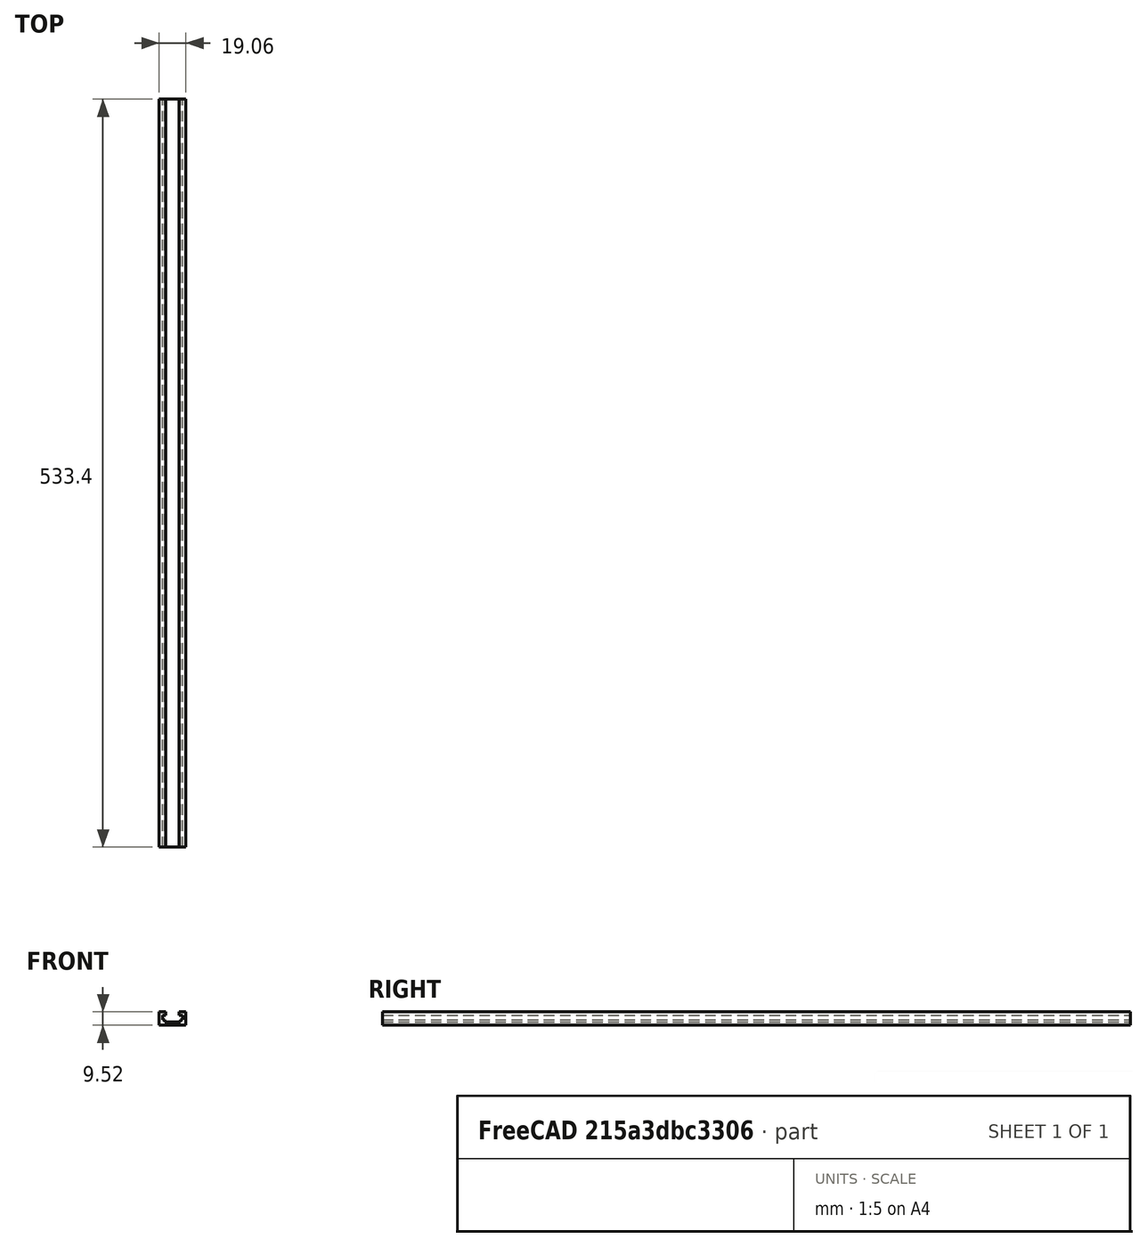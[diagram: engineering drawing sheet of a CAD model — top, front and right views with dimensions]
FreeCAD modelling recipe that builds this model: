
FCSTD DOCUMENT  (FreeCAD 0.20R29603 (Git))
Label: near_fence_top_t_track
License: All rights reserved
LicenseURL: http://en.wikipedia.org/wiki/All_rights_reserved
objects: Sketcher::SketchObject×4, PartDesign::Pocket×3, TechDraw::DrawProjGroupItem×2, PartDesign::Pad×1, PartDesign::Body×1, TechDraw::DrawSVGTemplate×1, TechDraw::DrawProjGroup×1, TechDraw::DrawViewDimension×1, TechDraw::DrawPage×1
note: 13 computed .brp shape members not serialized (recipe doc carries the construction recipe); baked Part::Feature solids carry a one-line shape summary decoded from their .brp

FEATURE [Sketcher::SketchObject] Sketch
  FullyConstrained = true
  MapMode = 5
  Placement = pos=(0,0,0) rot=(1,0,0;1.5708rad)
  Support = -> [XZ_Plane]
  sketch-geometry (5):
    g0: LineSegment StartX=-9.525 StartY=-4.7625 StartZ=0 EndX=-9.525 EndY=4.7625 EndZ=0
    g1: LineSegment StartX=-9.525 StartY=4.7625 StartZ=0 EndX=9.525 EndY=4.7625 EndZ=0
    g2: LineSegment StartX=9.525 StartY=4.7625 StartZ=0 EndX=9.525 EndY=-4.7625 EndZ=0
    g3: LineSegment StartX=9.525 StartY=-4.7625 StartZ=0 EndX=-9.525 EndY=-4.7625 EndZ=0
    g4: GeomPoint X=0 Y=0 Z=0
  constraints (12):
    c: Coincident(g0,g1)
    c: Coincident(g1,g2)
    c: Coincident(g2,g3)
    c: Coincident(g3,g0)
    c: Horizontal(g1)
    c: Horizontal(g3)
    c: Vertical(g0)
    c: Vertical(g2)
    c: Symmetric(g1,g0,g4)
    c: DistanceX(g1,g1) = 19.05
    c: DistanceY(g2,g2) = 9.525
    c: Coincident(g-1,g4)
FEATURE [PartDesign::Pad] Pad
  Direction = (0,-1,-2e-16)
  Length = 533.4
  Length2 = 10
  Placement = pos=(0,0,0) rot=(1,0,0;1.5708rad)
  Profile = -> Sketch
  ReferenceAxis = -> Sketch [N_Axis]
  Type = 0
FEATURE [Sketcher::SketchObject] Sketch001
  ExternalGeometry = -> [Pad]
  FullyConstrained = true
  MapMode = 5
  Placement = pos=(0,-533.4,-1.173e-13) rot=(1,0,0;1.5708rad)
  Support = -> [Pad]
  sketch-geometry (5):
    g0: LineSegment StartX=-4.7625 StartY=2.38125 StartZ=0 EndX=-4.7625 EndY=4.7625 EndZ=0
    g1: LineSegment StartX=-4.7625 StartY=4.7625 StartZ=0 EndX=4.7625 EndY=4.7625 EndZ=0
    g2: LineSegment StartX=4.7625 StartY=4.7625 StartZ=0 EndX=4.7625 EndY=2.38125 EndZ=0
    g3: LineSegment StartX=4.7625 StartY=2.38125 StartZ=0 EndX=-4.7625 EndY=2.38125 EndZ=0
    g4: GeomPoint X=0 Y=3.57187 Z=0
  constraints (12):
    c: Coincident(g0,g1)
    c: Coincident(g1,g2)
    c: Coincident(g2,g3)
    c: Coincident(g3,g0)
    c: Horizontal(g3)
    c: Vertical(g0)
    c: Vertical(g2)
    c: Symmetric(g1,g0,g4)
    c: Tangent(g1,g-3)
    c: DistanceX(g3,g3) = 9.525
    c: Distance(g2,g-4) = 7.14375
    c: PointOnObject(g4,g-2)
FEATURE [PartDesign::Pocket] Pocket
  BaseFeature = -> Pad
  Direction = (0,1,2e-16)
  Length = 5
  Length2 = 5
  Placement = pos=(0,0,0) rot=(1,0,0;1.5708rad)
  Profile = -> Sketch001
  ReferenceAxis = -> Sketch001 [N_Axis]
  Type = 1
FEATURE [Sketcher::SketchObject] Sketch002
  ExternalGeometry = -> [Pocket]
  FullyConstrained = true
  MapMode = 5
  Placement = pos=(0,-533.4,-1.173e-13) rot=(1,0,0;1.5708rad)
  Support = -> [Pocket]
  sketch-geometry (5):
    g0: LineSegment StartX=-7.14375 StartY=2.38125 StartZ=0 EndX=-7.14375 EndY=-0.79375 EndZ=0
    g1: LineSegment StartX=-7.14375 StartY=-0.79375 StartZ=0 EndX=7.14375 EndY=-0.79375 EndZ=0
    g2: LineSegment StartX=7.14375 StartY=-0.79375 StartZ=0 EndX=7.14375 EndY=2.38125 EndZ=0
    g3: LineSegment StartX=7.14375 StartY=2.38125 StartZ=0 EndX=-7.14375 EndY=2.38125 EndZ=0
    g4: GeomPoint X=0 Y=0.79375 Z=0
  constraints (12):
    c: Coincident(g0,g1)
    c: Coincident(g1,g2)
    c: Coincident(g2,g3)
    c: Coincident(g3,g0)
    c: Horizontal(g1)
    c: Vertical(g0)
    c: Vertical(g2)
    c: Symmetric(g1,g0,g4)
    c: Tangent(g3,g-3)
    c: PointOnObject(g4,g-2)
    c: Distance(g0,g-4) = 3.96875
    c: DistanceX(g1,g1) = 14.2875
FEATURE [PartDesign::Pocket] Pocket001
  BaseFeature = -> Pocket
  Direction = (0,1,2e-16)
  Length = 5
  Length2 = 5
  Placement = pos=(0,0,0) rot=(1,0,0;1.5708rad)
  Profile = -> Sketch002
  ReferenceAxis = -> Sketch002 [N_Axis]
  Type = 1
FEATURE [Sketcher::SketchObject] Sketch003
  ExternalGeometry = -> [Pocket001]
  FullyConstrained = true
  MapMode = 5
  Placement = pos=(0,-533.4,-1.173e-13) rot=(1,0,0;1.5708rad)
  Support = -> [Pocket001]
  sketch-geometry (5):
    g0: LineSegment StartX=-5.55625 StartY=-0.79375 StartZ=0 EndX=-5.55625 EndY=-2.38125 EndZ=0
    g1: LineSegment StartX=-5.55625 StartY=-2.38125 StartZ=0 EndX=5.55625 EndY=-2.38125 EndZ=0
    g2: LineSegment StartX=5.55625 StartY=-2.38125 StartZ=0 EndX=5.55625 EndY=-0.79375 EndZ=0
    g3: LineSegment StartX=5.55625 StartY=-0.79375 StartZ=0 EndX=-5.55625 EndY=-0.79375 EndZ=0
    g4: GeomPoint X=0 Y=-1.5875 Z=0
  constraints (12):
    c: Coincident(g0,g1)
    c: Coincident(g1,g2)
    c: Coincident(g2,g3)
    c: Coincident(g3,g0)
    c: Horizontal(g1)
    c: Vertical(g0)
    c: Vertical(g2)
    c: Symmetric(g1,g0,g4)
    c: DistanceX(g1,g1) = 11.1125
    c: PointOnObject(g4,g-2)
    c: DistanceY(g0,g0) = 1.5875
    c: Tangent(g-3,g3)
FEATURE [PartDesign::Pocket] Pocket002
  BaseFeature = -> Pocket001
  Direction = (0,1,2e-16)
  Length = 5
  Length2 = 5
  Placement = pos=(0,0,0) rot=(1,0,0;1.5708rad)
  Profile = -> Sketch003
  ReferenceAxis = -> Sketch003 [N_Axis]
  Type = 1
FEATURE [PartDesign::Body] Body
  Group = -> [Sketch,Pad,Sketch001,Pocket,Sketch002,Pocket001,Sketch003,Pocket002]
  Origin = -> Origin
  Tip = -> Pocket002
FEATURE [TechDraw::DrawSVGTemplate] Template
  Height = 297
  Orientation = 1
  Width = 420
FEATURE [TechDraw::DrawProjGroupItem] ProjItem  label="Front"
  CoarseView = false
  Direction = (0,0,1)
  Focus = 100
  HardHidden = false
  IsoCount = 0
  IsoHidden = false
  IsoVisible = false
  LockPosition = true
  Perspective = false
  Rotation = 0
  RotationVector = (0,1,0)
  Scale = 0.5
  ScaleType = 2
  SeamHidden = false
  SeamVisible = true
  SmoothHidden = false
  SmoothVisible = true
  Source = -> [Body]
  Type = 0
  X = 0
  XDirection = (0,1,0)
  Y = 0
FEATURE [TechDraw::DrawProjGroupItem] ProjItem001  label="FrontTopRight"
  CoarseView = false
  Direction = (-0.57735,0.57735,0.57735)
  Focus = 100
  HardHidden = false
  IsoCount = 0
  IsoHidden = false
  IsoVisible = false
  LockPosition = false
  Perspective = false
  Rotation = 0
  RotationVector = (1,0,0)
  Scale = 0.5
  ScaleType = 2
  SeamHidden = false
  SeamVisible = true
  SmoothHidden = false
  SmoothVisible = true
  Source = -> [Body]
  Type = 7
  X = -281.781
  XDirection = (0,0.707107,-0.707107)
  Y = -281.781
FEATURE [TechDraw::DrawProjGroup] ProjGroup
  Anchor = -> ProjItem
  AutoDistribute = true
  LockPosition = false
  ProjectionType = 0
  Rotation = 0
  Scale = 0.5
  ScaleType = 0
  Source = -> [Body]
  Views = -> [ProjItem,ProjItem001]
  X = 210
  Y = 148.5
  spacingX = 15.0812
  spacingY = 15.0812
FEATURE [TechDraw::DrawViewDimension] Dimension
  AngleOverride = false
  Arbitrary = false
  ArbitraryTolerances = false
  EqualTolerance = true
  ExtensionAngle = 0
  FormatSpec = %.2w
  FormatSpecOverTolerance = %+.2w
  FormatSpecUnderTolerance = %+.2w
  Inverted = false
  LineAngle = 0
  LockPosition = false
  MeasureType = 1
  OverTolerance = 0
  References2D = -> [ProjItem]
  Rotation = 0
  Scale = 0.5
  ScaleType = 0
  TheoreticalExact = false
  Type = 1
  UnderTolerance = 0
  X = -2.76504
  Y = -8.81891
FEATURE [TechDraw::DrawPage] Page
  KeepUpdated = true
  NextBalloonIndex = 1
  ProjectionType = 0
  Scale = 0.5
  Template = -> Template
  Views = -> [ProjGroup,Dimension]
